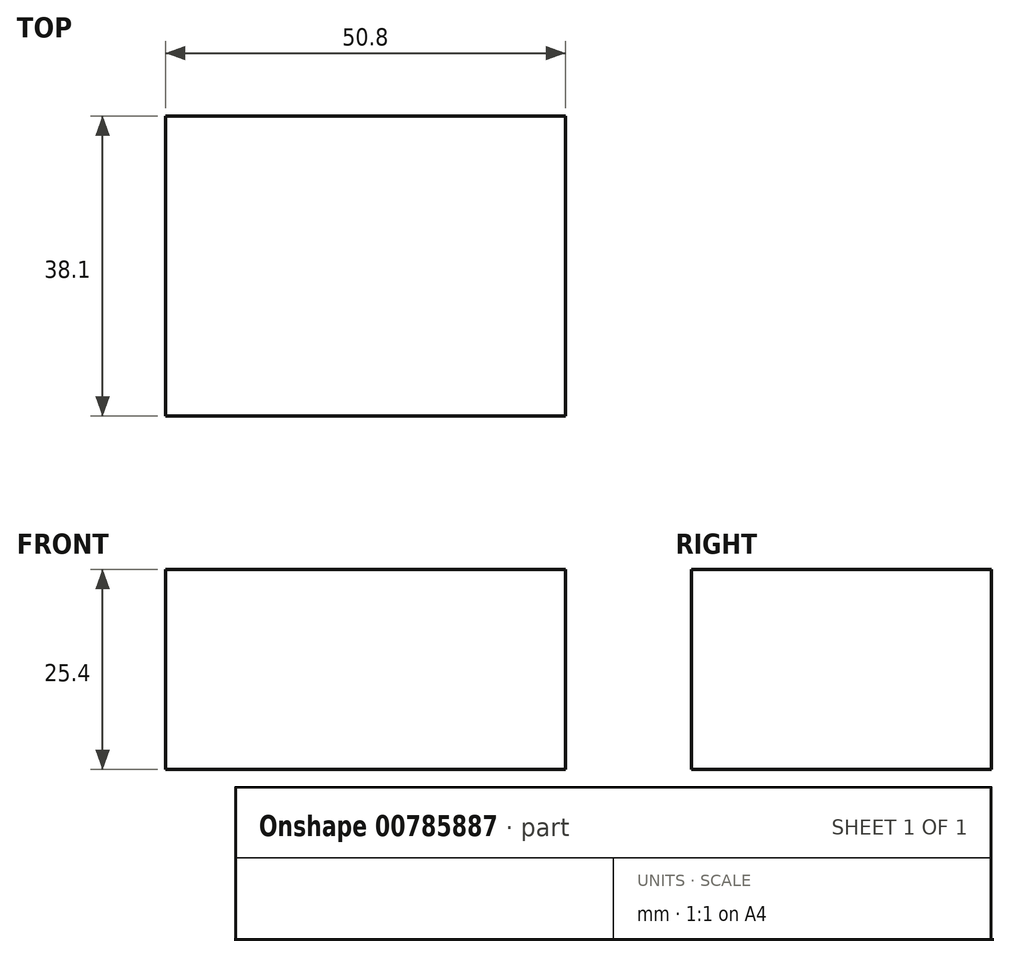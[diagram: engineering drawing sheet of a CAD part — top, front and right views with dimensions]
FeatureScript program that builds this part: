
annotation { "Feature Type Name" : "Feature", "Feature Type Description" : "" }
export const myFeature = defineFeature(function(context is Context, id is Id, definition is map)
    precondition{}
    {
        {
            var Q0;
            Q0=qCreatedBy(makeId("Front.planeOp"),FACE);
            var sketch = newSketch(context, id + "F0", { "sketchPlane" : qUnion([Q0])});
            skLineSegment(sketch, "E0", {"start": v(0, 0) * mm, "end": v(25.4, 0) * mm});
            skLineSegment(sketch, "E1", {"start": v(25.4, 25.4) * mm, "end": v(25.4, 0) * mm});
            skLineSegment(sketch, "E2", {"start": v(25.4, 25.4) * mm, "end": v(-25.4, 25.4) * mm});
            skLineSegment(sketch, "E3", {"start": v(-25.4, 25.4) * mm, "end": v(-23.1, 25.4) * mm});
            skLineSegment(sketch, "E4", {"start": v(-25.4, 25.4) * mm, "end": v(-25.4, 0) * mm});
            skLineSegment(sketch, "E5", {"start": v(-25.4, 0) * mm, "end": v(0, 0) * mm});
            skSolve(sketch);
        }
        {
            var Q0;
            Q0=makeQuery(id+"F0.imprint","IMPRINT",FACE,{"disambiguationData":[TD([[makeQuery(id+"F0.imprint","IMPRINT",EDGE,{"derivedFrom":sQuery(id+"F0.wireOp",EDGE,"E0")}),1.0]])]});
            extrude(context, id + "F1", {"entities" : qUnion([Q0]), "depth" : 38.1 * mm, "offsetDistance" : 25.4 * mm});
        }
    });
